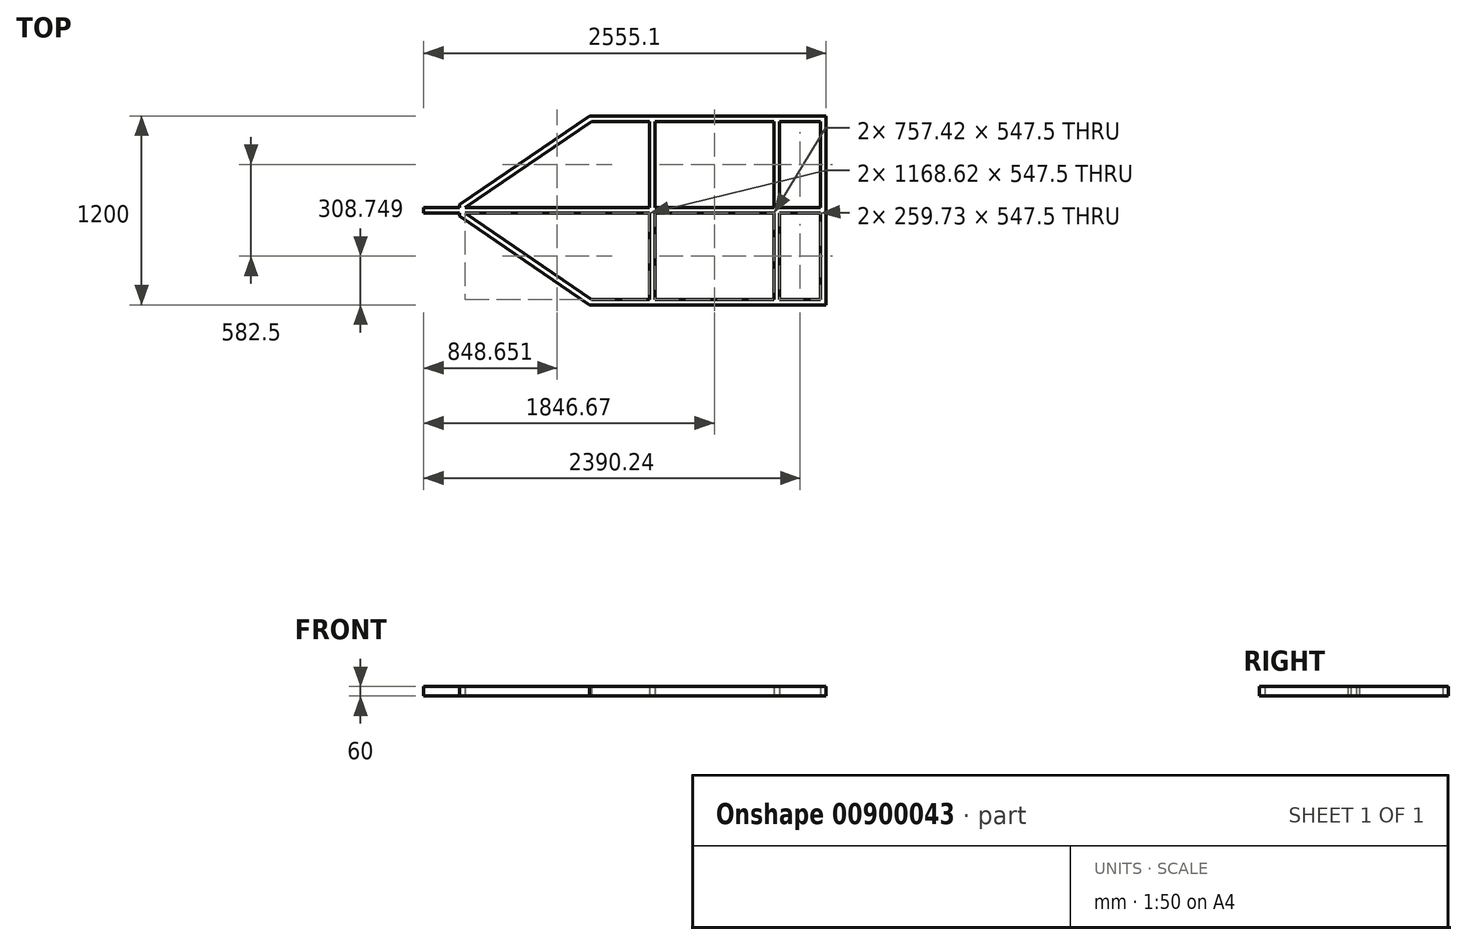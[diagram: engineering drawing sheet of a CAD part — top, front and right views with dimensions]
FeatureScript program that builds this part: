
annotation { "Feature Type Name" : "Feature", "Feature Type Description" : "" }
export const myFeature = defineFeature(function(context is Context, id is Id, definition is map)
    precondition{}
    {
        {
            var Q0;
            Q0=qCreatedBy(makeId("Top.planeOp"),FACE);
            var sketch = newSketch(context, id + "F0", { "sketchPlane" : qUnion([Q0])});
            skLineSegment(sketch, "E0", {"start": v(2.23, 709.72) * mm, "end": v(2.23, -490.28) * mm});
            skLineSegment(sketch, "E1", {"start": v(2.23, -490.28) * mm, "end": v(-1497.77, -490.28) * mm});
            skLineSegment(sketch, "E2", {"start": v(-1497.77, -490.28) * mm, "end": v(-2323.53, 73.74) * mm});
            skLineSegment(sketch, "E3", {"start": v(-2323.53, 73.74) * mm, "end": v(-2323.53, 92.26) * mm});
            skLineSegment(sketch, "E4", {"start": v(-2323.53, 145.7) * mm, "end": v(-1497.77, 709.72) * mm});
            skLineSegment(sketch, "E5", {"start": v(-1497.77, 709.72) * mm, "end": v(2.23, 709.72) * mm});
            skLineSegment(sketch, "E6.0", {"start": v(-2288.53, 127.22) * mm, "end": v(-1486.95, 674.72) * mm});
            skLineSegment(sketch, "E6.1", {"start": v(-32.77, 674.72) * mm, "end": v(-32.77, 127.22) * mm});
            skLineSegment(sketch, "E6.2", {"start": v(-32.77, -455.28) * mm, "end": v(-292.5, -455.28) * mm});
            skLineSegment(sketch, "E6.3", {"start": v(-1486.95, 674.72) * mm, "end": v(-1119.91, 674.72) * mm});
            skLineSegment(sketch, "E6.4", {"start": v(-1486.95, -455.28) * mm, "end": v(-2288.53, 92.22) * mm});
            skLineSegment(sketch, "E7", {"start": v(-327.5, 674.72) * mm, "end": v(-327.5, 127.22) * mm});
            skLineSegment(sketch, "E8", {"start": v(-292.5, -455.28) * mm, "end": v(-292.5, 92.22) * mm});
            skLineSegment(sketch, "E9", {"start": v(-1119.91, 674.72) * mm, "end": v(-1119.91, 127.22) * mm});
            skLineSegment(sketch, "E10", {"start": v(-1084.91, -455.28) * mm, "end": v(-1084.91, 92.22) * mm});
            skLineSegment(sketch, "E11", {"start": v(-2288.53, 127.22) * mm, "end": v(-1119.91, 127.22) * mm});
            skLineSegment(sketch, "E12", {"start": v(-2288.53, 92.22) * mm, "end": v(-1119.91, 92.22) * mm});
            skLineSegment(sketch, "E13", {"start": v(-2323.53, 127.22) * mm, "end": v(-2552.87, 127.22) * mm});
            skLineSegment(sketch, "E14", {"start": v(-2552.87, 127.22) * mm, "end": v(-2552.87, 92.56) * mm});
            skLineSegment(sketch, "E15", {"start": v(-2552.87, 92.56) * mm, "end": v(-2323.53, 92.26) * mm});
            skLineSegment(sketch, "E16.trimOffspring", {"start": v(-2323.53, 127.22) * mm, "end": v(-2323.53, 145.7) * mm});
            skLineSegment(sketch, "E17.trimOffspring", {"start": v(-1084.91, 127.22) * mm, "end": v(-1084.91, 674.72) * mm});
            skLineSegment(sketch, "E18.trimOffspring", {"start": v(-1084.91, 127.22) * mm, "end": v(-327.5, 127.22) * mm});
            skLineSegment(sketch, "E19.trimOffspring", {"start": v(-1119.91, 92.22) * mm, "end": v(-1119.91, -455.28) * mm});
            skLineSegment(sketch, "E20.trimOffspring", {"start": v(-1084.91, 92.22) * mm, "end": v(-327.5, 92.22) * mm});
            skLineSegment(sketch, "E21.trimOffspring", {"start": v(-292.5, 127.22) * mm, "end": v(-32.77, 127.22) * mm});
            skLineSegment(sketch, "E22.trimOffspring", {"start": v(-327.5, 92.22) * mm, "end": v(-327.5, -455.28) * mm});
            skLineSegment(sketch, "E23.trimOffspring", {"start": v(-292.5, 92.22) * mm, "end": v(-32.77, 92.22) * mm});
            skLineSegment(sketch, "E24.trimOffspring", {"start": v(-292.5, 127.22) * mm, "end": v(-292.5, 674.72) * mm});
            skLineSegment(sketch, "E25.trimOffspring", {"start": v(-32.77, 92.22) * mm, "end": v(-32.77, -455.28) * mm});
            skLineSegment(sketch, "E26.trimOffspring", {"start": v(-292.5, 674.72) * mm, "end": v(-32.77, 674.72) * mm});
            skLineSegment(sketch, "E27.trimOffspring", {"start": v(-1084.91, 674.72) * mm, "end": v(-327.5, 674.72) * mm});
            skLineSegment(sketch, "E28.trimOffspring", {"start": v(-327.5, -455.28) * mm, "end": v(-1084.91, -455.28) * mm});
            skLineSegment(sketch, "E29.trimOffspring", {"start": v(-1119.91, -455.28) * mm, "end": v(-1486.95, -455.28) * mm});
            skSolve(sketch);
        }
        {
            var Q0;
            Q0=makeQuery(id+"F0.imprint","IMPRINT",FACE,{"disambiguationData":[TD([[makeQuery(id+"F0.imprint","IMPRINT",EDGE,{"derivedFrom":sQuery(id+"F0.wireOp",EDGE,"E0")}),-1.0]])]});
            extrude(context, id + "F1", {"entities" : qUnion([Q0]), "depth" : 60 * mm, "offsetDistance" : 25 * mm});
        }
    });
